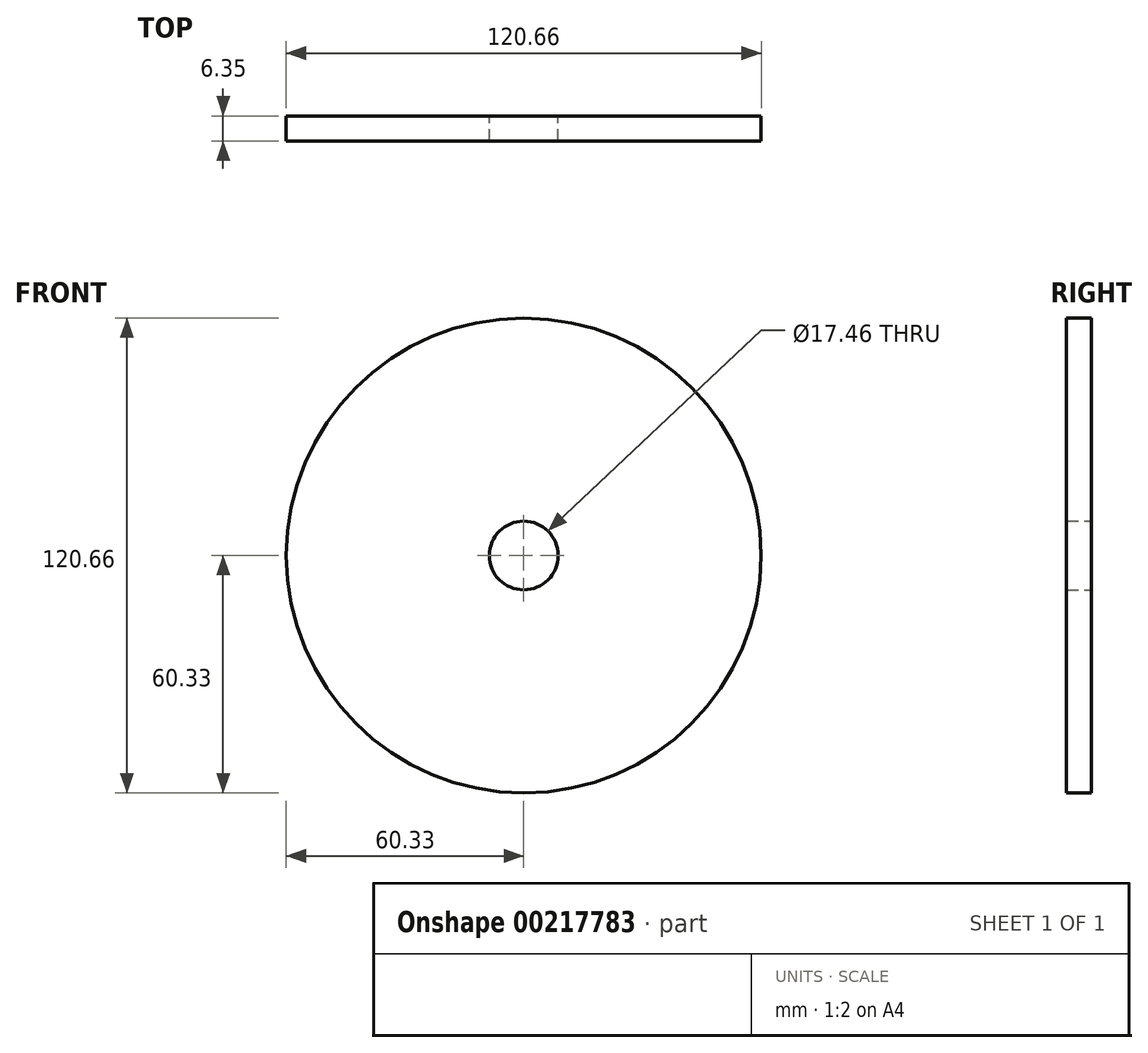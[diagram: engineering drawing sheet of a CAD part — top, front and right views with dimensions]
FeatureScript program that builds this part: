
annotation { "Feature Type Name" : "Feature", "Feature Type Description" : "" }
export const myFeature = defineFeature(function(context is Context, id is Id, definition is map)
    precondition{}
    {
        {
            var Q0;
            Q0=qCreatedBy(makeId("Front.planeOp"),FACE);
            var sketch = newSketch(context, id + "F0", { "sketchPlane" : qUnion([Q0])});
            skCircle(sketch, "E0", {"center": v(0, 0) * mm, "radius": 60.33 * mm});
            skCircle(sketch, "E1", {"center": v(0, 0) * mm, "radius": 8.73 * mm});
            skSolve(sketch);
        }
        {
            var Q0;
            Q0=makeQuery(id+"F0.imprint","IMPRINT",FACE,{"disambiguationData":[TD([[makeQuery(id+"F0.imprint","IMPRINT",EDGE,{"derivedFrom":sQuery(id+"F0.wireOp",EDGE,"E0")}),1.0]])]});
            extrude(context, id + "F1", {"entities" : qUnion([Q0]), "depth" : 6.35 * mm});
        }
    });
